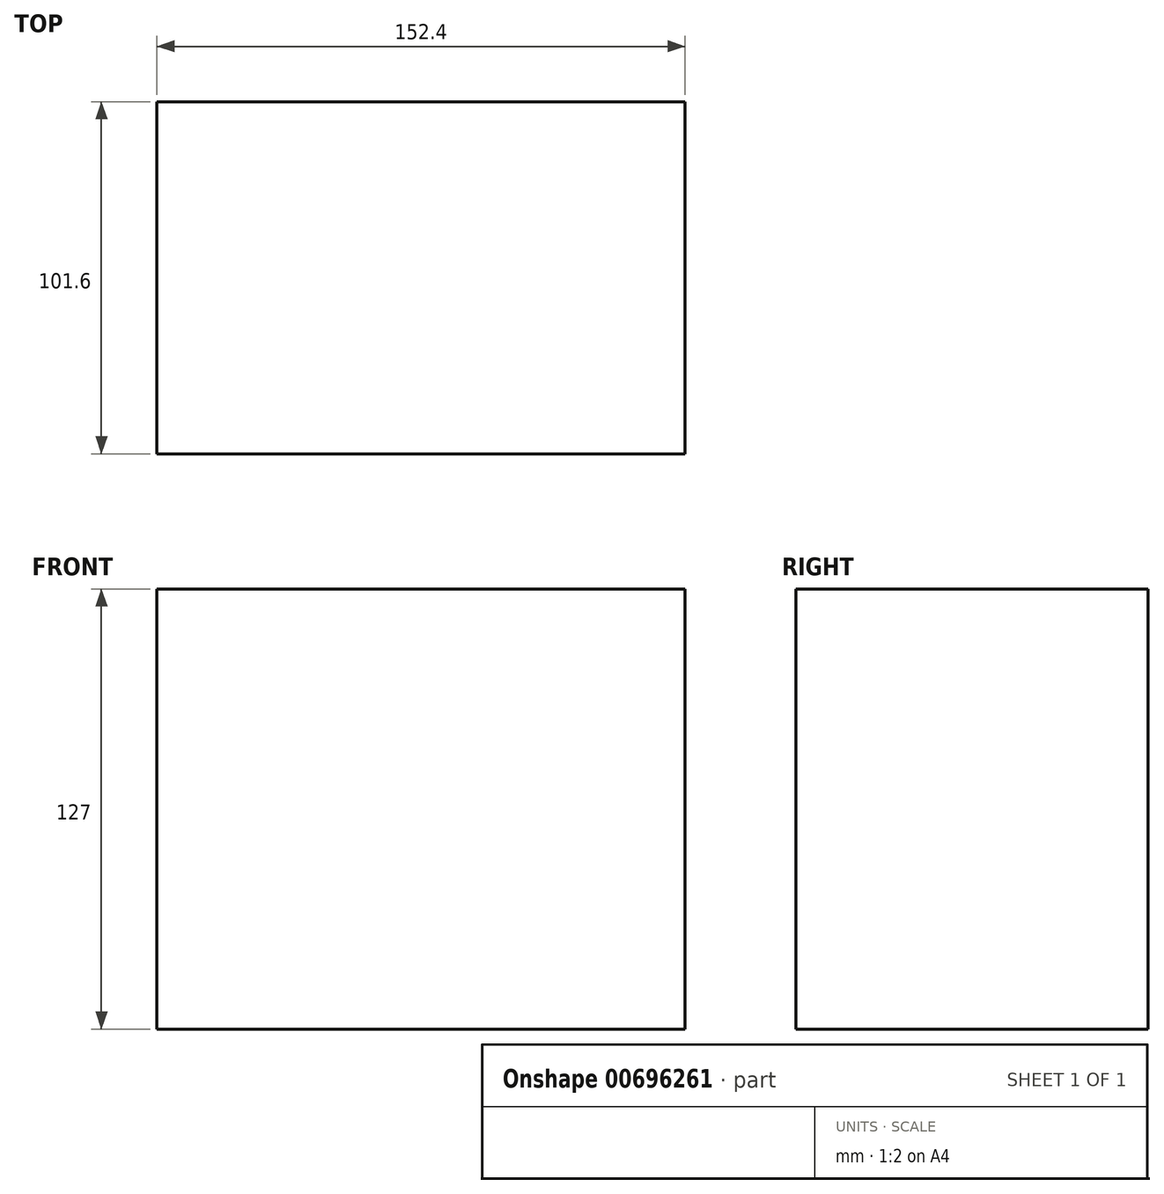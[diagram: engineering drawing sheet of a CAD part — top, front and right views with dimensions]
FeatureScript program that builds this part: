
annotation { "Feature Type Name" : "Feature", "Feature Type Description" : "" }
export const myFeature = defineFeature(function(context is Context, id is Id, definition is map)
    precondition{}
    {
        {
            var Q0;
            Q0=qCreatedBy(makeId("Front.planeOp"),FACE);
            var sketch = newSketch(context, id + "F0", { "sketchPlane" : qUnion([Q0])});
            skLineSegment(sketch, "E0", {"start": v(-59.13, 0) * mm, "end": v(93.27, 0) * mm});
            skLineSegment(sketch, "E1", {"start": v(-59.13, 0) * mm, "end": v(-59.13, 127) * mm});
            skLineSegment(sketch, "E2", {"start": v(93.27, 0) * mm, "end": v(93.27, 127) * mm});
            skLineSegment(sketch, "E3", {"start": v(93.27, 127) * mm, "end": v(-59.13, 127) * mm});
            skSolve(sketch);
        }
        {
            var Q0;
            Q0=makeQuery(id+"F0.imprint","IMPRINT",FACE,{"disambiguationData":[TD([[makeQuery(id+"F0.imprint","IMPRINT",EDGE,{"derivedFrom":sQuery(id+"F0.wireOp",EDGE,"E0")}),1.0]])]});
            extrude(context, id + "F1", {"entities" : qUnion([Q0]), "depth" : 101.6 * mm, "offsetDistance" : 25.4 * mm});
        }
    });
